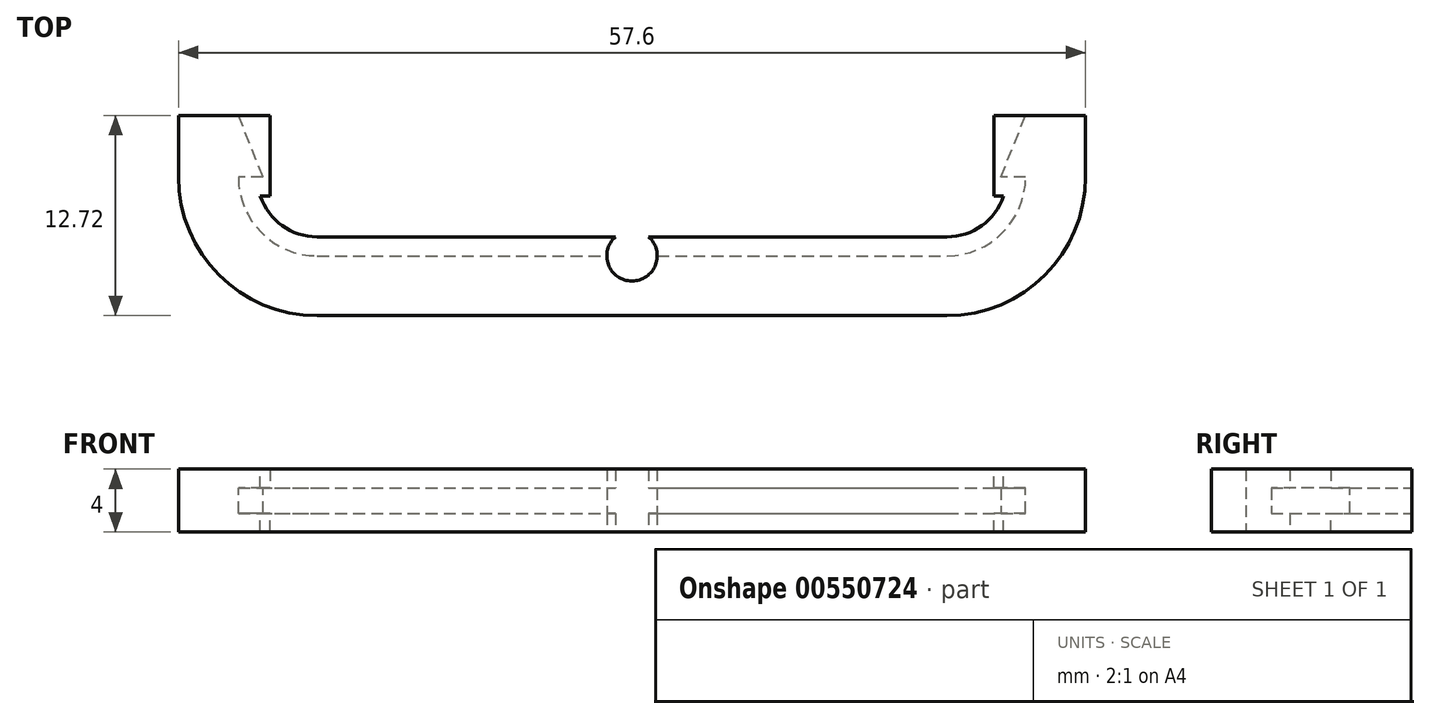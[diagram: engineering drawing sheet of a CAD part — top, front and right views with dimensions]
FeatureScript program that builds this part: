
annotation { "Feature Type Name" : "Feature", "Feature Type Description" : "" }
export const myFeature = defineFeature(function(context is Context, id is Id, definition is map)
    precondition{}
    {
        {
            var Q0;
            Q0=qCreatedBy(makeId("Right.planeOp"),FACE);
            var sketch = newSketch(context, id + "F0", { "sketchPlane" : qUnion([Q0])});
            skLineSegment(sketch, "E0", {"start": v(0, 0) * mm, "end": v(0, 2) * mm});
            skLineSegment(sketch, "E1", {"start": v(0, 2) * mm, "end": v(5, 2) * mm});
            skLineSegment(sketch, "E2", {"start": v(5, 2) * mm, "end": v(5, 0.8) * mm});
            skLineSegment(sketch, "E3", {"start": v(5, 0.8) * mm, "end": v(3.8, 0.8) * mm});
            skLineSegment(sketch, "E4", {"start": v(3.8, 0.8) * mm, "end": v(3.8, 0) * mm});
            skLineSegment(sketch, "E5.MirrorCS", {"start": v(0, 0) * mm, "end": v(0, -2) * mm});
            skLineSegment(sketch, "E6.MirrorCS", {"start": v(0, -2) * mm, "end": v(5, -2) * mm});
            skLineSegment(sketch, "E7.MirrorCS", {"start": v(3.8, -0.8) * mm, "end": v(3.8, 0) * mm});
            skLineSegment(sketch, "E8.MirrorCS", {"start": v(5, -0.8) * mm, "end": v(3.8, -0.8) * mm});
            skLineSegment(sketch, "E9.MirrorCS", {"start": v(5, -2) * mm, "end": v(5, -0.8) * mm});
            skLineSegment(sketch, "E10", {"start": v(3.8, 0.8) * mm, "end": v(3.8, 2.24) * mm, "construction": true});
            skSolve(sketch);
        }
        {
            var Q0;
            Q0=qCreatedBy(makeId("Top.planeOp"),FACE);
            var sketch = newSketch(context, id + "F1", { "sketchPlane" : qUnion([Q0])});
            skLineSegment(sketch, "E11", {"start": v(0, 0) * mm, "end": v(20, 0) * mm, "construction": true});
            skLineSegment(sketch, "E12", {"start": v(25, 8.8) * mm, "end": v(25, 13.8) * mm, "construction": true});
            skPoint(sketch, "E13.visualSharp", {"position": v(25, 0) * mm});
            skLineSegment(sketch, "E14", {"start": v(25, 8.8) * mm, "end": v(23, 8.8) * mm});
            skLineSegment(sketch, "E15", {"start": v(23, 8.8) * mm, "end": v(25, 13.8) * mm});
            skLineSegment(sketch, "E16", {"start": v(0, 3.8) * mm, "end": v(20, 3.8) * mm});
            skArc(sketch, "E17", {"start": v(20, 3.8) * mm, "mid": v(23.54, 5.26) * mm, "end": v(25, 8.8) * mm});
            skLineSegment(sketch, "E18.MirrorCS", {"start": v(0, 3.8) * mm, "end": v(-20, 3.8) * mm});
            skArc(sketch, "E19.MirrorCS", {"start": v(-20, 3.8) * mm, "mid": v(-23.54, 5.26) * mm, "end": v(-25, 8.8) * mm});
            skLineSegment(sketch, "E20.MirrorCS", {"start": v(-25, 8.8) * mm, "end": v(-23, 8.8) * mm});
            skLineSegment(sketch, "E21.MirrorCS", {"start": v(-23, 8.8) * mm, "end": v(-25, 13.8) * mm});
            skSolve(sketch);
        }
        {
            var Q0;
            Q0=makeQuery(id+"F0.imprint","IMPRINT",FACE,{"disambiguationData":[TD([[makeQuery(id+"F0.imprint","IMPRINT",EDGE,{"derivedFrom":sQuery(id+"F0.wireOp",EDGE,"E0")}),-1.0]])]});
            var Q1;
            Q1=sQuery(id+"F1.wireOp",EDGE,"E18.MirrorCS");
            var Q2;
            Q2=sQuery(id+"F1.wireOp",EDGE,"E19.MirrorCS");
            var Q3;
            Q3=sQuery(id+"F1.wireOp",EDGE,"E20.MirrorCS");
            var Q4;
            Q4=sQuery(id+"F1.wireOp",EDGE,"E16");
            var Q5;
            Q5=sQuery(id+"F1.wireOp",EDGE,"E17");
            var Q6;
            Q6=sQuery(id+"F1.wireOp",EDGE,"E14");
            sweep(context, id + "F2", {"profiles" : qUnion([Q0]), "path" : qUnion([Q1, Q2, Q3, Q4, Q5, Q6])});
        }
        {
            var Q0;
            Q0=makeQuery(id+"F2.opSweep","SWEPT_FACE",FACE,{"disambiguationData":[OSD([sQuery(id+"F0.wireOp",EDGE,"E6.MirrorCS"),sQuery(id+"F1.wireOp",EDGE,"a626e529-b565-4477-b8c0-75d9263467f50.MirrorCS")])]});
            var sketch = newSketch(context, id + "F3", { "sketchPlane" : qUnion([Q0])});
            skCircle(sketch, "E22", {"center": v(0, -3.8) * mm, "radius": 1.6 * mm});
            skCircle(sketch, "E23", {"center": v(0, -3.8) * mm, "radius": 3.2 * mm});
            skSolve(sketch);
        }
        {
            var Q0;
            {var subQ0=sQuery(id+"F3.wireOp",EDGE,"E22");var subQ1=makeQuery(id+"F2.opSweep","SWEPT_EDGE",EDGE,{"disambiguationData":[OSD([sQuery(id+"F0.wireOp",EDGE,"E6.MirrorCS"),sQuery(id+"F0.wireOp",EDGE,"E9.MirrorCS"),sQuery(id+"F1.wireOp",EDGE,"E16")])]});var subQ2=makeQuery(id+"F3.imprint","INTERSECT",VERTEX,{"disambiguationData":[OD(0.0)],"derivedFrom":[subQ1,subQ0]});Q0=makeQuery(id+"F3.imprint","IMPRINT",FACE,{"disambiguationData":[TD([[makeQuery(id+"F3.imprint","IMPRINT",EDGE,{"disambiguationData":[TD([[subQ2,1.0]])],"derivedFrom":subQ0}),1.0]])]});}
            extrude(context, id + "F4", {"entities" : qUnion([Q0]), "operationType" : NewBodyOperationType.REMOVE, "oppositeDirection" : true, "depth" : 25 * mm, "offsetDistance" : 25 * mm});
        }
        {
            assignVariable(context, id + "F5", {"name" : "Breite", "anyValue" : 0.38});
        }
        {
            var Q0;
            Q0=makeQuery(id+"F2.opSweep","SWEPT_FACE",FACE,{"disambiguationData":[OSD([sQuery(id+"F0.wireOp",EDGE,"E0"),sQuery(id+"F0.wireOp",EDGE,"E5.MirrorCS"),sQuery(id+"F1.wireOp",EDGE,"E20.MirrorCS")])]});
            var Q1;
            Q1=makeQuery(id+"F2.opSweep","SWEPT_FACE",FACE,{"disambiguationData":[OSD([sQuery(id+"F0.wireOp",EDGE,"E0"),sQuery(id+"F0.wireOp",EDGE,"E5.MirrorCS"),sQuery(id+"F1.wireOp",EDGE,"E14")])]});
            extrude(context, id + "F6", {"entities" : qUnion([Q0, Q1]), "operationType" : NewBodyOperationType.ADD, "depth" : (0.5 - getVariable(context, 'Breite')) * mm, "offsetDistance" : 25 * mm});
        }
        {
            var Q0;
            Q0=makeQuery(id+"F6.opExtrude","CAP_FACE",FACE,{"disambiguationData":[OSD([sQuery(id+"F0.wireOp",EDGE,"E0"),sQuery(id+"F0.wireOp",EDGE,"E1"),sQuery(id+"F0.wireOp",EDGE,"E5.MirrorCS"),sQuery(id+"F0.wireOp",EDGE,"E6.MirrorCS"),sQuery(id+"F1.wireOp",VERTEX,"E14.start"),sQuery(id+"F1.wireOp",VERTEX,"E14.end"),sQuery(id+"F1.wireOp",EDGE,"E14")])],"isStart":false});
            var sketch = newSketch(context, id + "F7", { "sketchPlane" : qUnion([Q0])});
            skLineSegment(sketch, "E24", {"start": v(-23, 0.8) * mm, "end": v(-25, 0.8) * mm});
            skLineSegment(sketch, "E25", {"start": v(-25, 0.8) * mm, "end": v(-25, -0.8) * mm});
            skLineSegment(sketch, "E26", {"start": v(-25, -0.8) * mm, "end": v(-23, -0.8) * mm});
            skLineSegment(sketch, "E27.MirrorCS", {"start": v(25, -0.8) * mm, "end": v(23, -0.8) * mm});
            skLineSegment(sketch, "E28.MirrorCS", {"start": v(25, 0.8) * mm, "end": v(25, -0.8) * mm});
            skLineSegment(sketch, "E29.MirrorCS", {"start": v(23, 0.8) * mm, "end": v(25, 0.8) * mm});
            skSolve(sketch);
        }
        {
            var Q0;
            {var subQ0=sQuery(id+"F7.wireOp",EDGE,"E24");Q0=makeQuery(id+"F7.imprint","IMPRINT",FACE,{"disambiguationData":[TD([[makeQuery(id+"F7.imprint","IMPRINT",EDGE,{"derivedFrom":subQ0}),1.0]])]});}
            var Q1;
            Q1=sQuery(id+"F1.wireOp",EDGE,"E15");
            sweep(context, id + "F8", {"operationType" : NewBodyOperationType.REMOVE, "profiles" : qUnion([Q0]), "path" : qUnion([Q1])});
        }
        {
            var Q0;
            Q0=makeQuery(id+"F6.opExtrude","CAP_FACE",FACE,{"disambiguationData":[OSD([sQuery(id+"F0.wireOp",EDGE,"E0"),sQuery(id+"F0.wireOp",EDGE,"E5.MirrorCS"),sQuery(id+"F1.wireOp",EDGE,"E20.MirrorCS")])],"isStart":false});
            var sketch = newSketch(context, id + "F9", { "sketchPlane" : qUnion([Q0])});
            skLineSegment(sketch, "E30", {"start": v(23, -0.8) * mm, "end": v(25, -0.8) * mm});
            skLineSegment(sketch, "E31", {"start": v(25, -0.8) * mm, "end": v(25, 0.8) * mm});
            skLineSegment(sketch, "E32", {"start": v(25, 0.8) * mm, "end": v(23, 0.8) * mm});
            skSolve(sketch);
        }
        {
            var Q0;
            Q0 = qSketchRegion(id + "F7", true);
            var Q1;
            {var subQ0=sQuery(id+"F9.wireOp",EDGE,"E30");Q1=makeQuery(id+"F9.imprint","IMPRINT",FACE,{"disambiguationData":[TD([[makeQuery(id+"F9.imprint","IMPRINT",EDGE,{"derivedFrom":subQ0}),1.0]])]});}
            var Q2;
            Q2=sQuery(id+"F1.wireOp",EDGE,"E21.MirrorCS");
            sweep(context, id + "F10", {"operationType" : NewBodyOperationType.REMOVE, "profiles" : qUnion([Q0, Q1]), "path" : qUnion([Q2])});
        }
    });
